# Revit family: ONIZGG - All Opened cases - Linked Data
name_source: partatom
category: Mechanical Equipment
units: mm (PartAtom-declared; Revit-internal decimal feet)

## family parameters
Always vertical = Yes
Cut with Voids When Loaded = No
OmniClass Number = 23.40.40.11.17
OmniClass Title = Refrigerated Cases
Part Type = Normal
Room Calculation Point = No
Round Connector Dimension = Use Radius
Shared = No
Work Plane-Based = Yes

## types (8) — shared parameters
BOTTOM ELECTRICAL = Yes
BOTTOM REFRIGERATION PIPING = Yes
Case Type/Application = Closed Low Temp Case
Certifications = NSF 7, UL471, CSA
DATE = 04/28/2016
DRAIN PIPING = Yes
Default Elevation = 48"
Description = ONIZGG - Island case
EQUIPMENT DESCRIPTION = ONIZGG - Island case
EQUIPMENT MARK = ONIZGG
GLASS = Glass
Height = 35 3/4"
How Many Defrosts Per Day = 2
Island Discharge Air Velocity (FPM) = 255 FPM
Island Electric Fail-Safe = 35 (Min)
Island Electric Termination Temp (F°) = 47 °F
Island Hot Gas Fail-Safe (Min) = 10 (Min)
Island Hot Gas Termination Temp (F°) = 60 °F
Island Run-Off Time (Min) = 13-15 (Min)
Island Tank/Drain Heater Amps = 0 A
Island Tank/Drain Heater Watts = 15 W
Item Description = ONIZGG - Island case
LF STD END = Yes
Legend Number = ONIZGG
Manufacturer = HILL PHOENIX
Model = ONIZGG
PAINTED METAL UPPER SHELF = PAINTED SHELVES
REAR REFRIGERATION PIPING = Yes
REFRIGERATION PIPING = COPPER PIPE
RT STD END = Yes
STAINLESS STEEL = GALVANIZED STEEL
TOP ELECTRICAL = Yes
TOP REFRIGERATION PIPING = Yes
URL = http://www.hillphoenix.com
Width = 44 1/8"

## per-type parameters (varying)
| type | CENTER LINE | Island  Case Length | Island 208V Defrost Heaters Amps | Island 208V Defrost Heaters Watts | Island 240 Defrost Heaters Amps | Island 240 Defrost Heaters Watts | Island Anti-Condensate Heaters Amps | Island Anti-Condensate Heaters Watts | Island Application | Island BTUH Conventional | Island BTUH Parallel | Island Discharge Air(°F) | Island Evaporator (°F) | Island Fans Per Case | Island High Efficiency Fans Amps | Island High Efficiency Fans Watts | Island Superheat @ Bulb Set Point (°F) | Length |
| 05' - Open - Low Temp | 30" | 60" | 7 A | 1500 A | 8 A | 1997 W | 2 A | 203 W | Opened Low Temp Case | 553 | 530 | -10 °F | -22 °F | 2 | 0 A | 22 W | 3-5 °F | 60" |
| 08' - Open - Low Temp | 48" | 96" | 12 A | 2400 A | 13 A | 3195 W | 3 A | 305 W | Opened Low Temp Case | 553 | 530 | -10 °F | -22 °F | 3 | 0 A | 33 W | 3-5 °F | 96" |
| 12' - Open - Low Temp | 72" | 144" | 17 A | 3600 A | 20 A | 4795 W | 3 A | 417 W | Opened LowTemp Case | 553 | 530 | -10 °F | -22 °F | 4 | 1 A | 44 W | 3-5 °F | 144" |
| 06' - Open - Low Temp | 36" | 72" | 9 A | 1800 A | 10 A | 2396 W | 2 A | 271 W | Opened Low Temp Case | 553 | 530 | -10 °F | -22 °F | 2 | 0 A | 22 W | 3-5 °F | 72" |
| 05' - Open - Medium Temp | 30" | 60" | 7 A | 1500 A | 8 A | 1997 W | 2 A | 203 W | Opened MediumTemp Case | 290 | 284 | 29 °F | 22 °F | 2 | 0 A | 22 W | 6-8 °F | 60" |
| 06' - Open - Medium Temp | 36" | 72" | 9 A | 1800 A | 10 A | 2396 W | 2 A | 271 W | Opened MediumTemp Case | 290 | 284 | 29 °F | 22 °F | 2 | 0 A | 22 W | 6-8 °F | 72" |
| 08' - Open - Medium Temp | 48" | 96" | 12 A | 2400 A | 13 A | 3195 W | 3 A | 305 W | Opened MediumTemp Case | 290 | 284 | 29 °F | 22 °F | 3 | 0 A | 33 W | 6-8 °F | 96" |
| 12' - Open - Medium Temp | 72" | 144" | 17 A | 3600 A | 20 A | 4795 W | 3 A | 417 W | Opened MediumTemp Case | 290 | 284 | 29 °F | 22 °F | 4 | 1 A | 44 W | 6-8 °F | 144" |

## geometry (parser evidence)
native form markers: Blend x8, Sweep x2
no freeform markers — native parametric forms only
